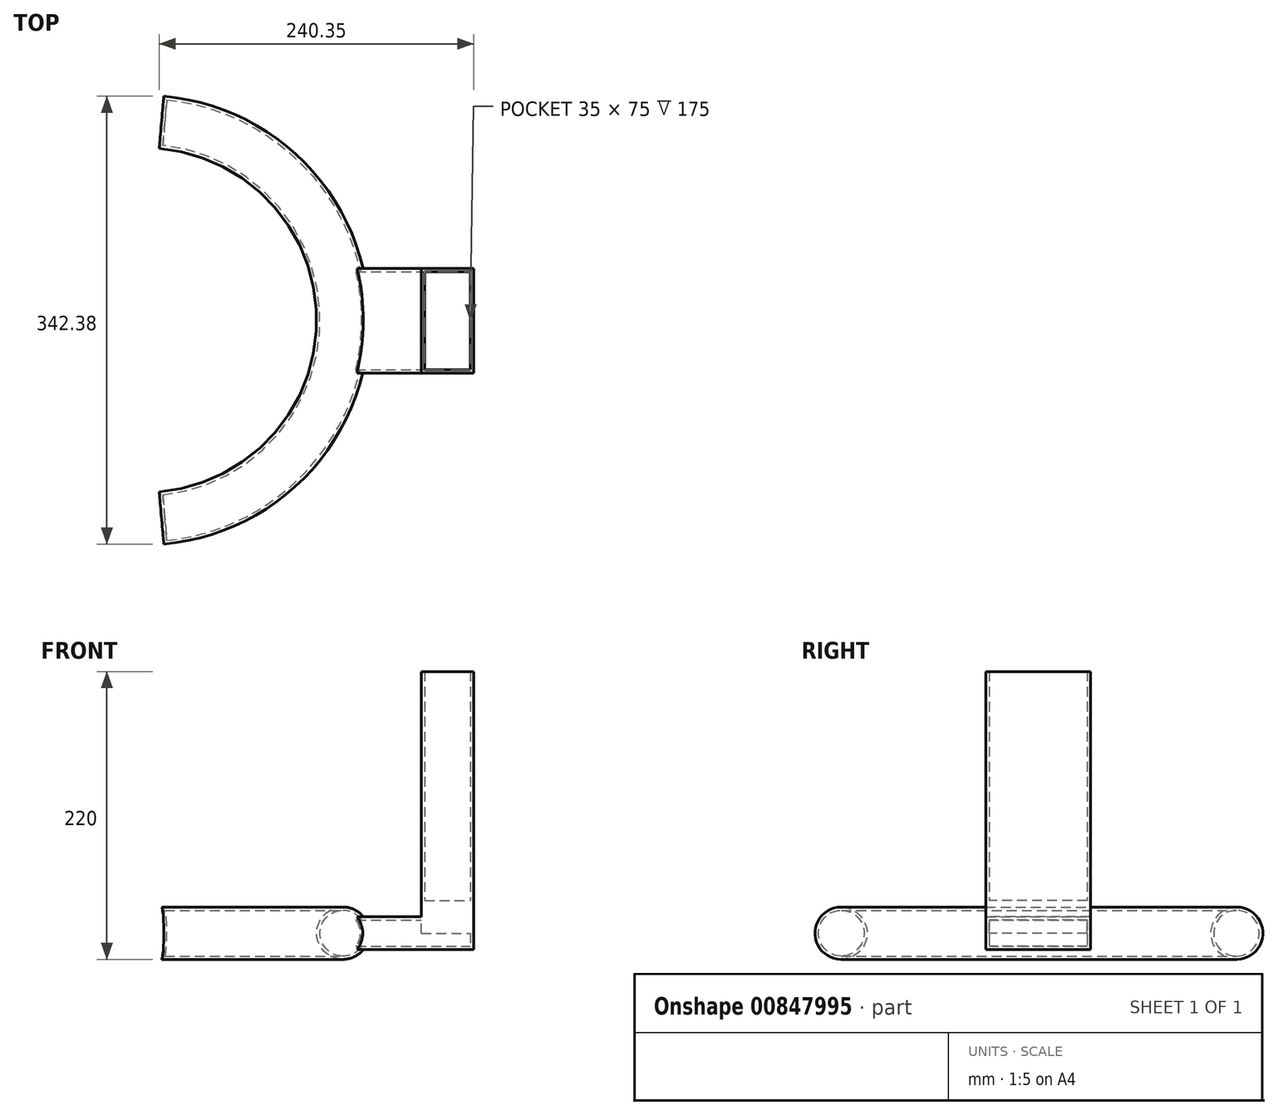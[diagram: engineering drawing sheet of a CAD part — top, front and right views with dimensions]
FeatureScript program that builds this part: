
annotation { "Feature Type Name" : "Feature", "Feature Type Description" : "" }
export const myFeature = defineFeature(function(context is Context, id is Id, definition is map)
    precondition{}
    {
        {
            var Q0;
            Q0=qCreatedBy(makeId("Front.planeOp"),FACE);
            var sketch = newSketch(context, id + "F0", { "sketchPlane" : qUnion([Q0])});
            skCircle(sketch, "E0", {"center": v(0, 0) * mm, "radius": 20 * mm});
            skLineSegment(sketch, "E1", {"start": v(-151.84, 59.35) * mm, "end": v(-151.84, -55.8) * mm});
            skSolve(sketch);
        }
        {
            var Q0;
            Q0=makeQuery(id+"F0.imprint","IMPRINT",FACE,{"disambiguationData":[TD([[makeQuery(id+"F0.imprint","IMPRINT",EDGE,{"derivedFrom":sQuery(id+"F0.wireOp",EDGE,"E0")}),1.0]])]});
            var Q1;
            Q1=sQuery(id+"F0.wireOp",EDGE,"E1");
            revolve(context, id + "F1", {"surfaceOperationType" : NewSurfaceOperationType.NEW, "entities" : qUnion([Q0]), "axis" : qUnion([Q1]), "revolveType" : RevolveType.SYMMETRIC, "angle" : 170 * degree});
        }
        {
            var Q0;
            Q0=qCreatedBy(makeId("Top.planeOp"),FACE);
            var sketch = newSketch(context, id + "F2", { "sketchPlane" : qUnion([Q0])});
            skLineSegment(sketch, "E2.bottom", {"start": v(0, 0) * mm, "end": v(60, 0) * mm});
            skLineSegment(sketch, "E2.top", {"start": v(0, 39.38) * mm, "end": v(60, 39.38) * mm});
            skLineSegment(sketch, "E2.left", {"start": v(0, 0) * mm, "end": v(0, 39.38) * mm});
            skLineSegment(sketch, "E2.right", {"start": v(60, 0) * mm, "end": v(60, 39.38) * mm});
            skLineSegment(sketch, "E3.top", {"start": v(0, -40.62) * mm, "end": v(60, -40.62) * mm});
            skLineSegment(sketch, "E3.left", {"start": v(0, 0) * mm, "end": v(0, -40.62) * mm});
            skLineSegment(sketch, "E3.right", {"start": v(60, 0) * mm, "end": v(60, -40.62) * mm});
            skLineSegment(sketch, "E4.bottom", {"start": v(60, 39.38) * mm, "end": v(100, 39.38) * mm});
            skLineSegment(sketch, "E4.top", {"start": v(60, -40.62) * mm, "end": v(100, -40.62) * mm});
            skLineSegment(sketch, "E4.left", {"start": v(60, 39.38) * mm, "end": v(60, -40.62) * mm});
            skLineSegment(sketch, "E4.right", {"start": v(100, 39.38) * mm, "end": v(100, -40.62) * mm});
            skSolve(sketch);
        }
        {
            var Q0;
            Q0 = qSketchRegion(id + "F2", true);
            extrude(context, id + "F3", {"entities" : qUnion([Q0]), "operationType" : NewBodyOperationType.ADD, "endBound" : BoundingType.SYMMETRIC, "depth" : 25 * mm, "offsetDistance" : 25 * mm});
        }
        {
            var Q0;
            {var subQ3=sQuery(id+"F2.wireOp",EDGE,"E4.bottom");Q0=makeQuery(id+"F2.imprint","IMPRINT",FACE,{"disambiguationData":[TD([[makeQuery(id+"F2.imprint","IMPRINT",EDGE,{"derivedFrom":subQ3}),-1.0]])]});}
            extrude(context, id + "F4", {"entities" : qUnion([Q0]), "operationType" : NewBodyOperationType.ADD, "depth" : 200 * mm, "offsetDistance" : 25 * mm});
        }
        {
            var Q0;
            Q0=makeQuery(id+"F4.opExtrude","CAP_FACE",FACE,{"disambiguationData":[OSD([sQuery(id+"F2.wireOp",EDGE,"E4.bottom"),sQuery(id+"F2.wireOp",EDGE,"E4.top"),sQuery(id+"F2.wireOp",EDGE,"E4.left"),sQuery(id+"F2.wireOp",EDGE,"E4.right")])],"isStart":false});
            shell(context, id + "F5", {"entities" : qUnion([Q0]), "thickness" : 2.5 * mm});
        }
        {
            var Q0;
            {var subQ3=sQuery(id+"F2.wireOp",EDGE,"E4.bottom");Q0=makeQuery(id+"F2.imprint","IMPRINT",FACE,{"disambiguationData":[TD([[makeQuery(id+"F2.imprint","IMPRINT",EDGE,{"derivedFrom":subQ3}),-1.0]])]});}
            extrude(context, id + "F6", {"entities" : qUnion([Q0]), "operationType" : NewBodyOperationType.ADD, "depth" : 25 * mm, "offsetDistance" : 25 * mm});
        }
    });
